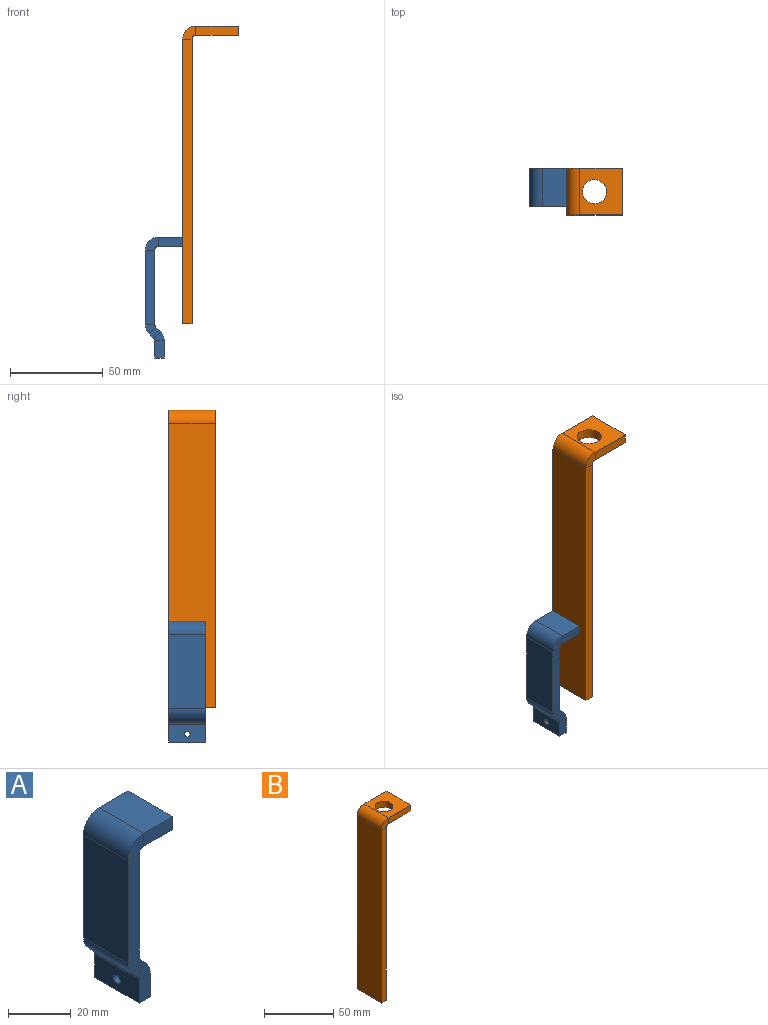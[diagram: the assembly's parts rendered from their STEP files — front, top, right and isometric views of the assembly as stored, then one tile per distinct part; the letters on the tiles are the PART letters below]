
ASSEMBLY  parts=2 mates=1
PART A: 31 faces, bbox 20x20x65 mm
  f0: plane 13x5mm, normal (0,1,0), area 65mm2, adj f2,f3,f4,f28
  f1: plane 13x5mm, normal (0,-1,0), area 65mm2, adj f2,f3,f4,f27
  f2: plane 20x5mm, normal (1,0,0), area 100mm2, adj f0,f1,f3,f4
  f3: plane 20x13mm, normal (0,0,1), area 260mm2, adj f0,f1,f2,f29
  f4: plane 20x13mm, normal (0,0,-1), area 260mm2, adj f0,f1,f2,f30
  f5: plane 40.1x5mm, normal (0,1,0), area 200.5mm2, adj f7,f8,f24,f28
  f6: plane 40.1x5mm, normal (0,-1,0), area 200.5mm2, adj f7,f8,f23,f27
  f7: plane 40.1x20mm, normal (-1,0,0), area 802mm2, adj f5,f6,f25,f29
  f8: plane 40.1x20mm, normal (1,0,0), area 802mm2, adj f5,f6,f26,f30
  f9: plane 5.9x5.9mm, normal (0,1,0), area 16.7mm2, adj f11,f12,f20,f24
  f10: plane 5.9x5.9mm, normal (0,-1,0), area 16.7mm2, adj f11,f12,f19,f23
  f11: plane 20x2.36mm, normal (-0.71,0,-0.71), area 66.9mm2, adj f9,f10,f22,f25
  f12: plane 20x2.36mm, normal (0.71,0,0.71), area 66.9mm2, adj f9,f10,f21,f26
  f13: plane 9.17x5mm, normal (0,1,0), area 45.9mm2, adj f14,f17,f18,f20
  f14: plane 20x5mm, normal (0,0,-1), area 100mm2, adj f13,f15,f17,f18
  f15: plane 9.17x5mm, normal (0,-1,0), area 45.9mm2, adj f14,f17,f18,f19
  f16: cylinder r=1.5mm len=5mm, axis (-1,0,0), area 47.1mm2, adj f17,f18
  f17: plane 20x9.17mm, normal (-1,0,0), area 176.4mm2, adj f13,f14,f15,f16,f22
  f18: plane 20x9.17mm, normal (1,0,0), area 176.4mm2, adj f13,f14,f15,f16,f21
  f19: plane 5.59x4.95mm, normal (0,-1,0), area 17.7mm2, adj f10,f15,f21,f22
  f20: plane 5.59x4.95mm, normal (0,1,0), area 17.7mm2, adj f9,f13,f21,f22
  f21: cylinder r=7mm len=20mm, axis (0,-1,0), area 110mm2, adj f12,f18,f19,f20
  f22: cylinder r=2mm len=20mm, axis (0,-1,0), area 31.4mm2, adj f11,f17,f19,f20
  f23: plane 5.59x4.95mm, normal (0,-1,0), area 17.7mm2, adj f6,f10,f25,f26
  f24: plane 5.59x4.95mm, normal (0,1,0), area 17.7mm2, adj f5,f9,f25,f26
  f25: cylinder r=7mm len=20mm, axis (0,-1,0), area 110mm2, adj f7,f11,f23,f24
  f26: cylinder r=2mm len=20mm, axis (0,-1,0), area 31.4mm2, adj f8,f12,f23,f24
  f27: plane 7x7mm, normal (0,-1,0), area 35.3mm2, adj f1,f6,f29,f30
  f28: plane 7x7mm, normal (0,1,0), area 35.3mm2, adj f0,f5,f29,f30
  f29: cylinder r=7mm len=20mm, axis (0,-1,0), area 219.9mm2, adj f3,f7,f27,f28
  f30: cylinder r=2mm len=20mm, axis (0,-1,0), area 62.8mm2, adj f4,f8,f27,f28
PART B: 15 faces, bbox 30x25x160 mm
  f0: plane 153x5mm, normal (0,1,0), area 765mm2, adj f1,f3,f4,f12
  f1: plane 25x5mm, normal (0,0,-1), area 125mm2, adj f0,f2,f3,f4
  f2: plane 153x5mm, normal (0,-1,0), area 765mm2, adj f1,f3,f4,f11
  f3: plane 153x25mm, normal (-1,0,0), area 3825mm2, adj f0,f1,f2,f13
  f4: plane 153x25mm, normal (1,0,0), area 3825mm2, adj f0,f1,f2,f14
  f5: plane 23x5mm, normal (0,1,0), area 115mm2, adj f8,f9,f10,f12
  f6: plane 23x5mm, normal (0,-1,0), area 115mm2, adj f8,f9,f10,f11
  f7: cylinder r=6.5mm len=13mm, axis (0,0,1), area 204.2mm2, adj f9,f10
  f8: plane 25x5mm, normal (1,0,0), area 125mm2, adj f5,f6,f9,f10
  f9: plane 25x23mm, normal (0,0,1), area 442.3mm2, adj f5,f6,f7,f8,f13
  f10: plane 25x23mm, normal (0,0,-1), area 442.3mm2, adj f5,f6,f7,f8,f14
  f11: plane 7x7mm, normal (0,-1,0), area 35.3mm2, adj f2,f6,f13,f14
  f12: plane 7x7mm, normal (0,1,0), area 35.3mm2, adj f0,f5,f13,f14
  f13: cylinder r=7mm len=25mm, axis (0,-1,0), area 274.9mm2, adj f3,f9,f11,f12
  f14: cylinder r=2mm len=25mm, axis (0,-1,0), area 78.5mm2, adj f4,f10,f11,f12
PLACE A t=(-29.03,-5.12,-82.41)mm
PLACE B t=(-9.03,-5.12,31.09)mm
MATE fastened B.f3 <-> A.f2  axis (-1,0,0) through (-9.03,-5.12,-52.41)mm
